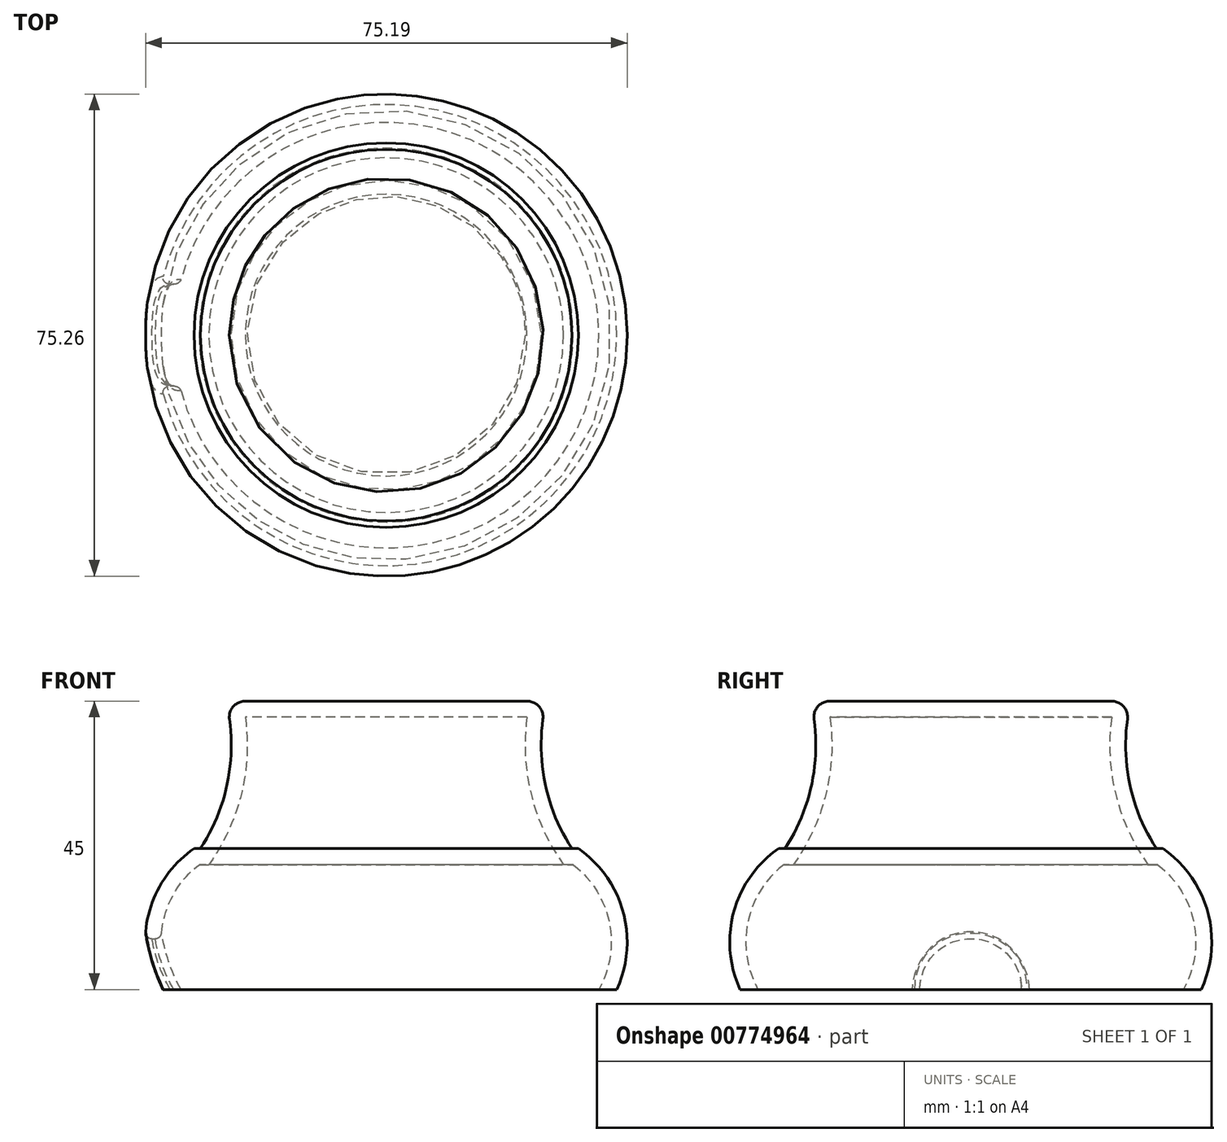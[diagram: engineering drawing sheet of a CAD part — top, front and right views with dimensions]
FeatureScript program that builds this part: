
annotation { "Feature Type Name" : "Feature", "Feature Type Description" : "" }
export const myFeature = defineFeature(function(context is Context, id is Id, definition is map)
    precondition{}
    {
        {
            var Q0;
            Q0=qCreatedBy(makeId("Front.planeOp"),FACE);
            var sketch = newSketch(context, id + "F0", { "sketchPlane" : qUnion([Q0])});
            skLineSegment(sketch, "E0", {"start": v(0, 0) * mm, "end": v(-36, 0) * mm});
            skArc(sketch, "E1", {"start": v(-30, 22) * mm, "mid": v(-37, 12.1) * mm, "end": v(-36, 0) * mm});
            skLineSegment(sketch, "E2", {"start": v(-30, 22) * mm, "end": v(-29, 22) * mm});
            skArc(sketch, "E3", {"start": v(-29, 22) * mm, "mid": v(-24.63, 33.09) * mm, "end": v(-25, 45) * mm});
            skLineSegment(sketch, "E4", {"start": v(-25, 45) * mm, "end": v(0, 45) * mm});
            skLineSegment(sketch, "E5", {"start": v(0, 45) * mm, "end": v(0, 0) * mm});
            skSolve(sketch);
        }
        {
            var Q0;
            Q0=makeQuery(id+"F0.imprint","IMPRINT",FACE,{"disambiguationData":[TD([[makeQuery(id+"F0.imprint","IMPRINT",EDGE,{"derivedFrom":sQuery(id+"F0.wireOp",EDGE,"E0")}),-1.0]])]});
            var Q1;
            Q1=sQuery(id+"F0.wireOp",EDGE,"E5");
            revolve(context, id + "F1", {"surfaceOperationType" : NewSurfaceOperationType.NEW, "entities" : qUnion([Q0]), "axis" : qUnion([Q1]), "revolveType" : RevolveType.FULL});
        }
        {
            var Q0;
            Q0=makeQuery(id+"F1.opRevolve","SWEPT_FACE",FACE,{"disambiguationData":[OSD([sQuery(id+"F0.wireOp",EDGE,"E0")])]});
            shell(context, id + "F2", {"entities" : qUnion([Q0]), "thickness" : 2.5 * mm});
        }
        {
            var Q0;
            Q0=makeQuery(id+"F1.opRevolve","SWEPT_EDGE",EDGE,{"disambiguationData":[OSD([sQuery(id+"F0.wireOp",EDGE,"E3"),sQuery(id+"F0.wireOp",EDGE,"E4")])]});
            fillet(context, id + "F3", {"entities" : qUnion([Q0]), "radius" : 2.48 * mm, "tangentPropagation" : true, "allowEdgeOverflow" : false});
        }
        {
            var Q0;
            Q0=qCreatedBy(makeId("Right.planeOp"),FACE);
            var sketch = newSketch(context, id + "F4", { "sketchPlane" : qUnion([Q0])});
            skCircle(sketch, "E6", {"center": v(0, 0) * mm, "radius": 7.94 * mm});
            skSolve(sketch);
        }
        {
            var Q0;
            Q0=makeQuery(id+"F4.imprint","IMPRINT",FACE,{"disambiguationData":[TD([[makeQuery(id+"F4.imprint","IMPRINT",EDGE,{"derivedFrom":sQuery(id+"F4.wireOp",EDGE,"E6")}),1.0]])]});
            var Q1;
            Q1=sQuery(id+"F4.wireOp",EDGE,"E6");
            extrude(context, id + "F5", {"entities" : qUnion([Q0]), "operationType" : NewBodyOperationType.REMOVE, "surfaceEntities" : qUnion([Q1]), "oppositeDirection" : true, "depth" : 121.4 * mm, "offsetDistance" : 25 * mm});
        }
        {
            var Q0;
            Q0=makeQuery(id+"F5.boolean.opBoolean","INTERSECT",EDGE,{"derivedFrom":[makeQuery(id+"F1.opRevolve","SWEPT_FACE",FACE,{"disambiguationData":[OSD([sQuery(id+"F0.wireOp",EDGE,"E1")])]}),makeQuery(id+"F5.opExtrude","SWEPT_FACE",FACE,{"disambiguationData":[OSD([sQuery(id+"F4.wireOp",EDGE,"E6")])]})]});
            var Q1;
            Q1=makeQuery(id+"F5.boolean.opBoolean","INTERSECT",EDGE,{"derivedFrom":[makeQuery(id+"F2.opShell","OFFSET_FACE",FACE,{"disambiguationData":[OSD([sQuery(id+"F0.wireOp",EDGE,"E1")])]}),makeQuery(id+"F5.opExtrude","SWEPT_FACE",FACE,{"disambiguationData":[OSD([sQuery(id+"F4.wireOp",EDGE,"E6")])]})]});
            fillet(context, id + "F6", {"entities" : qUnion([Q0, Q1]), "radius" : 1 * mm, "tangentPropagation" : true, "allowEdgeOverflow" : false});
        }
    });
